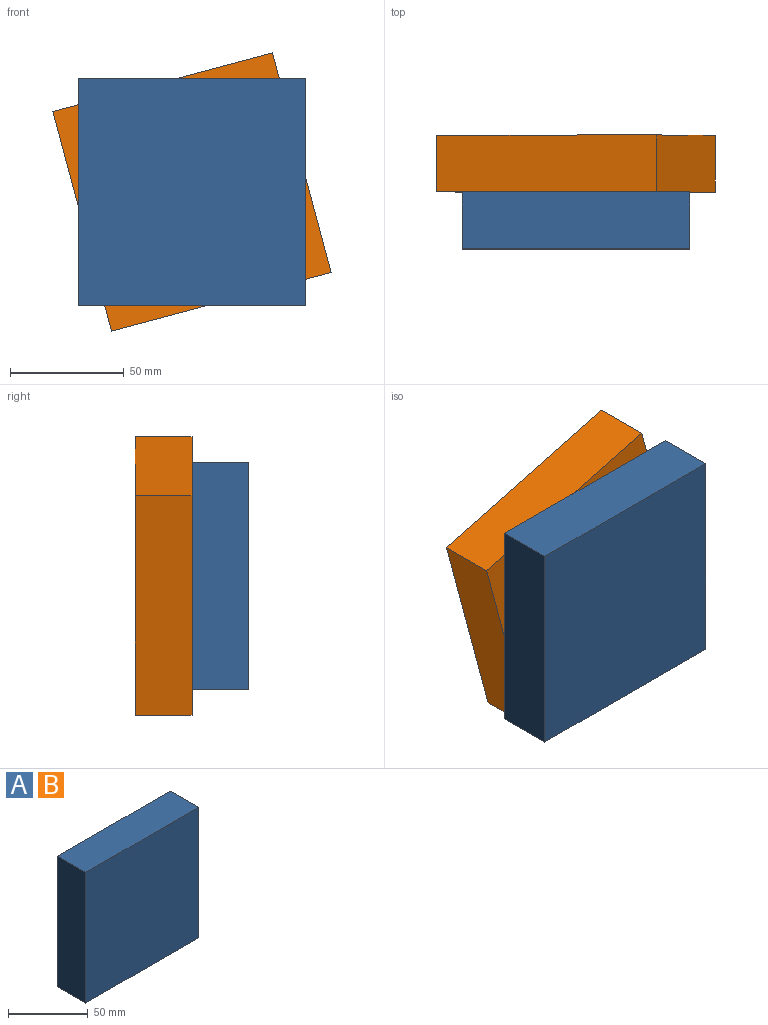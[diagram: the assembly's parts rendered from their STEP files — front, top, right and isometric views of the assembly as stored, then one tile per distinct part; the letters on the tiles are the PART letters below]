
ASSEMBLY  parts=2 mates=1
PART A: 6 faces, bbox 100x25x100 mm
  f0: plane 100x25mm, normal (0,0,-1), area 2500mm2, adj f1,f3,f4,f5
  f1: plane 100x25mm, normal (1,0,0), area 2500mm2, adj f0,f2,f4,f5
  f2: plane 100x25mm, normal (0,0,1), area 2500mm2, adj f1,f3,f4,f5
  f3: plane 100x25mm, normal (-1,0,0), area 2500mm2, adj f0,f2,f4,f5
  f4: plane 100x100mm, normal (0,-1,0), area 10000mm2, adj f0,f1,f2,f3
  f5: plane 100x100mm, normal (0,1,0), area 10000mm2, adj f0,f1,f2,f3
PART B: same geometry as A
PLACE A t=(-141.19,4.39,209.41)mm
PLACE B rot(axis=(0.99,0,0.13),180deg) t=(-93.06,4.39,-156.17)mm
MATE pin_slot B.f5 <-> A.f5  axis (0,-1,0) through (-99.37,4.39,28.96)mm
